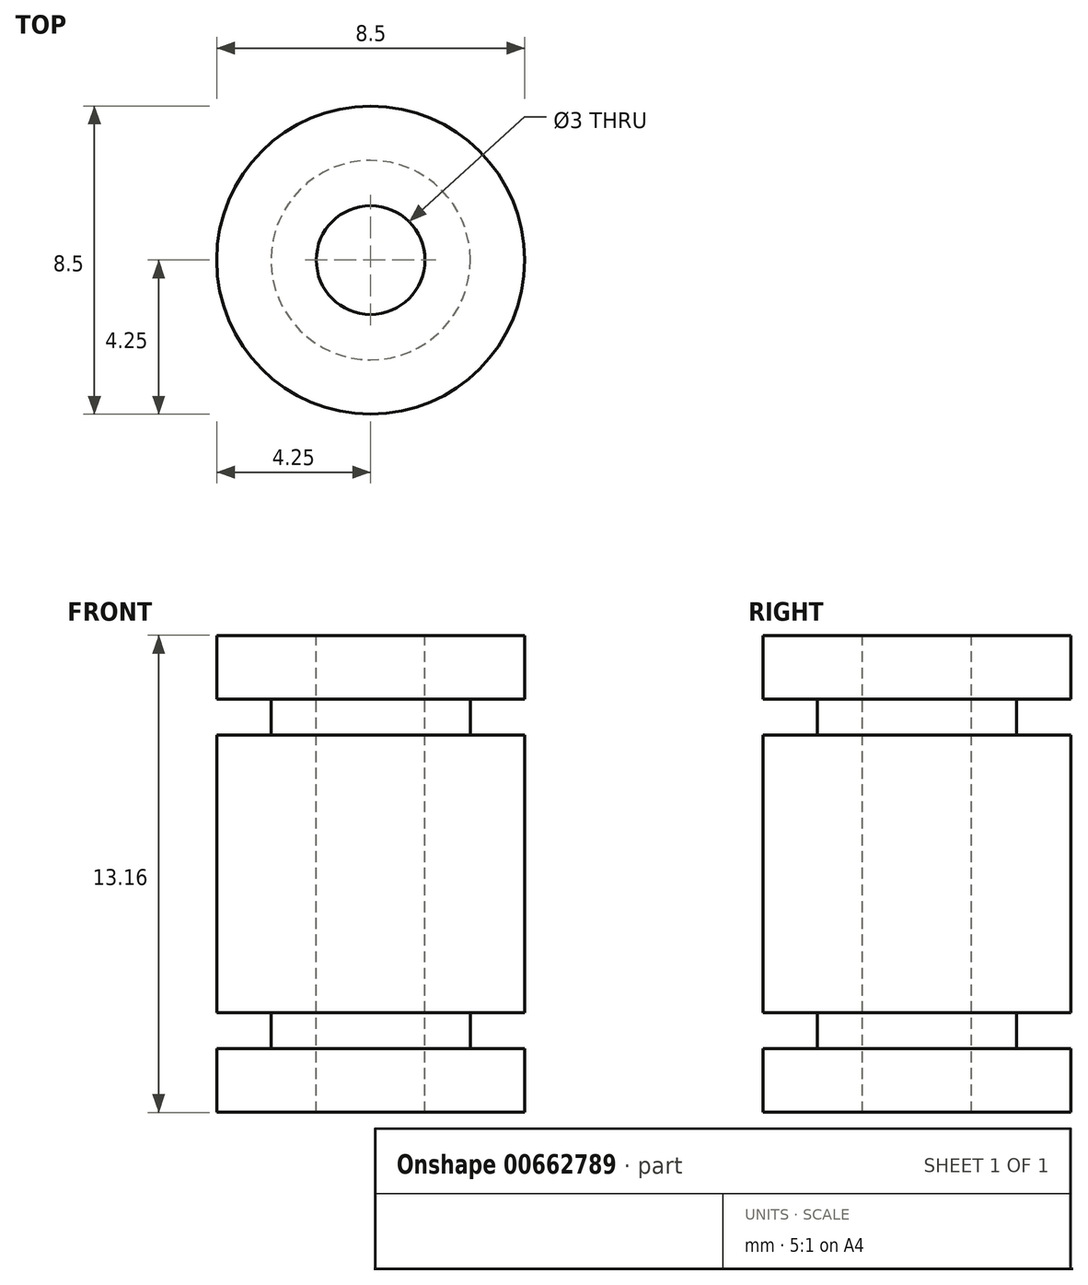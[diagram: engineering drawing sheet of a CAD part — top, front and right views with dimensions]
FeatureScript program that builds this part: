
annotation { "Feature Type Name" : "Feature", "Feature Type Description" : "" }
export const myFeature = defineFeature(function(context is Context, id is Id, definition is map)
    precondition{}
    {
        {
            var Q0;
            Q0=qCreatedBy(makeId("Front.planeOp"),FACE);
            var sketch = newSketch(context, id + "F0", { "sketchPlane" : qUnion([Q0])});
            skLineSegment(sketch, "E0", {"start": v(0, 6.58) * mm, "end": v(-4.25, 6.58) * mm});
            skLineSegment(sketch, "E1", {"start": v(-4.25, 6.58) * mm, "end": v(-4.25, 4.82) * mm});
            skLineSegment(sketch, "E2", {"start": v(-4.25, 4.83) * mm, "end": v(-2.75, 4.83) * mm});
            skLineSegment(sketch, "E3", {"start": v(-2.75, 4.82) * mm, "end": v(-2.75, 3.83) * mm});
            skLineSegment(sketch, "E4", {"start": v(-2.75, 3.83) * mm, "end": v(-4.25, 3.83) * mm});
            skLineSegment(sketch, "E5", {"start": v(-4.25, 3.82) * mm, "end": v(-4.25, 0) * mm});
            skLineSegment(sketch, "E6", {"start": v(0, 6.57) * mm, "end": v(0, 0) * mm, "construction": true});
            skLineSegment(sketch, "E7.MirrorCS", {"start": v(0, -6.57) * mm, "end": v(0, 0) * mm, "construction": true});
            skLineSegment(sketch, "E8.MirrorCS", {"start": v(0, -6.58) * mm, "end": v(-4.25, -6.58) * mm});
            skLineSegment(sketch, "E9.MirrorCS", {"start": v(-4.25, -6.58) * mm, "end": v(-4.25, -4.82) * mm});
            skLineSegment(sketch, "E10.MirrorCS", {"start": v(-4.25, -4.83) * mm, "end": v(-2.75, -4.83) * mm});
            skLineSegment(sketch, "E11.MirrorCS", {"start": v(-2.75, -4.82) * mm, "end": v(-2.75, -3.83) * mm});
            skLineSegment(sketch, "E12.MirrorCS", {"start": v(-2.75, -3.83) * mm, "end": v(-4.25, -3.83) * mm});
            skLineSegment(sketch, "E13.MirrorCS", {"start": v(-4.25, -3.82) * mm, "end": v(-4.25, 0) * mm});
            skLineSegment(sketch, "E14", {"start": v(-1.5, 6.58) * mm, "end": v(-1.5, -6.58) * mm});
            skSolve(sketch);
        }
        {
            var Q0;
            Q0=makeQuery(id+"F0.imprint","IMPRINT",FACE,{"disambiguationData":[TD([[makeQuery(id+"F0.imprint","IMPRINT",EDGE,{"derivedFrom":sQuery(id+"F0.wireOp",EDGE,"E0")}),1.0]])]});
            var Q1;
            Q1=sQuery(id+"F0.wireOp",EDGE,"E6");
            revolve(context, id + "F1", {"entities" : qUnion([Q0]), "axis" : qUnion([Q1]), "revolveType" : RevolveType.FULL});
        }
    });
